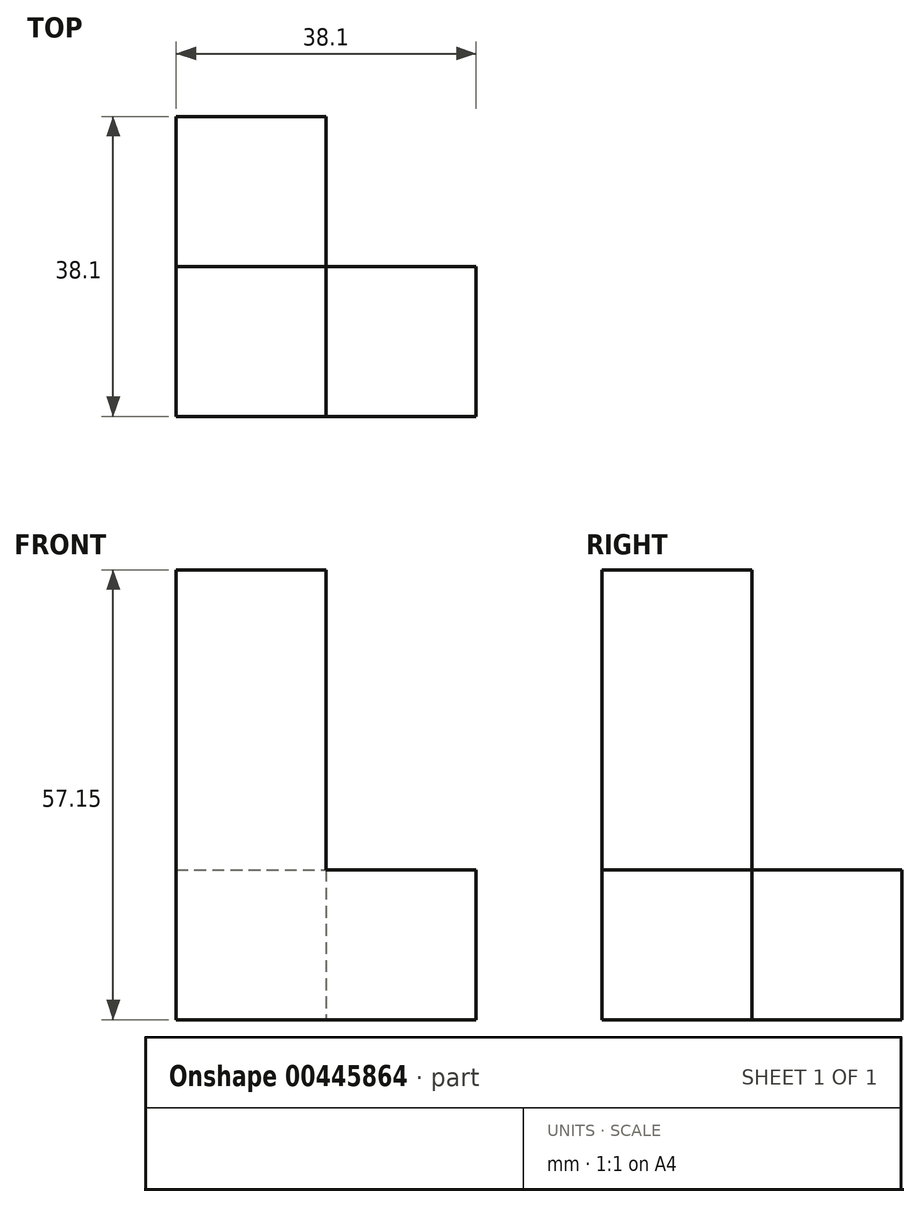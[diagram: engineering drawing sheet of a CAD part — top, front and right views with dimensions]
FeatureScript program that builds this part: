
annotation { "Feature Type Name" : "Feature", "Feature Type Description" : "" }
export const myFeature = defineFeature(function(context is Context, id is Id, definition is map)
    precondition{}
    {
        {
            var Q0;
            Q0=qCreatedBy(makeId("Top.planeOp"),FACE);
            var sketch = newSketch(context, id + "F0", { "sketchPlane" : qUnion([Q0])});
            skLineSegment(sketch, "E0.bottom", {"start": v(0, 0) * mm, "end": v(19.05, 0) * mm});
            skLineSegment(sketch, "E0.top", {"start": v(0, 19.05) * mm, "end": v(19.05, 19.05) * mm});
            skLineSegment(sketch, "E0.left", {"start": v(0, 0) * mm, "end": v(0, 19.05) * mm});
            skLineSegment(sketch, "E0.right", {"start": v(19.05, 0) * mm, "end": v(19.05, 19.05) * mm});
            skLineSegment(sketch, "E1.top", {"start": v(0, 38.1) * mm, "end": v(19.05, 38.1) * mm});
            skLineSegment(sketch, "E1.left", {"start": v(0, 19.05) * mm, "end": v(0, 38.1) * mm});
            skLineSegment(sketch, "E1.right", {"start": v(19.05, 19.05) * mm, "end": v(19.05, 38.1) * mm});
            skLineSegment(sketch, "E2.bottom", {"start": v(19.05, 0) * mm, "end": v(38.1, 0) * mm});
            skLineSegment(sketch, "E2.top", {"start": v(19.05, 19.05) * mm, "end": v(38.1, 19.05) * mm});
            skLineSegment(sketch, "E2.right", {"start": v(38.1, 0) * mm, "end": v(38.1, 19.05) * mm});
            skSolve(sketch);
        }
        {
            var Q0;
            Q0=makeQuery(id+"F0.imprint","IMPRINT",FACE,{"disambiguationData":[TD([[makeQuery(id+"F0.imprint","IMPRINT",EDGE,{"derivedFrom":sQuery(id+"F0.wireOp",EDGE,"E2.bottom")}),1.0]])]});
            var Q1;
            Q1=makeQuery(id+"F0.imprint","IMPRINT",FACE,{"disambiguationData":[TD([[makeQuery(id+"F0.imprint","IMPRINT",EDGE,{"derivedFrom":sQuery(id+"F0.wireOp",EDGE,"E0.bottom")}),1.0]])]});
            var Q2;
            Q2=makeQuery(id+"F0.imprint","IMPRINT",FACE,{"disambiguationData":[TD([[makeQuery(id+"F0.imprint","IMPRINT",EDGE,{"derivedFrom":sQuery(id+"F0.wireOp",EDGE,"E0.top")}),1.0]])]});
            extrude(context, id + "F1", {"entities" : qUnion([Q0, Q1, Q2]), "depth" : 19.05 * mm});
        }
        {
            var Q0;
            Q0=makeQuery(id+"F1.opExtrude","CAP_FACE",FACE,{"disambiguationData":[OSD([sQuery(id+"F0.wireOp",EDGE,"E0.bottom"),sQuery(id+"F0.wireOp",EDGE,"E0.left"),sQuery(id+"F0.wireOp",EDGE,"E1.top"),sQuery(id+"F0.wireOp",EDGE,"E1.left"),sQuery(id+"F0.wireOp",EDGE,"E1.right"),sQuery(id+"F0.wireOp",EDGE,"E2.bottom"),sQuery(id+"F0.wireOp",EDGE,"E2.top"),sQuery(id+"F0.wireOp",EDGE,"E2.right")])],"isStart":false});
            var sketch = newSketch(context, id + "F2", { "sketchPlane" : qUnion([Q0])});
            skLineSegment(sketch, "E3.bottom", {"start": v(0, 0) * mm, "end": v(19.05, 0) * mm});
            skLineSegment(sketch, "E3.top", {"start": v(0, 19.05) * mm, "end": v(19.05, 19.05) * mm});
            skLineSegment(sketch, "E3.left", {"start": v(0, 0) * mm, "end": v(0, 19.05) * mm});
            skLineSegment(sketch, "E3.right", {"start": v(19.05, 0) * mm, "end": v(19.05, 19.05) * mm});
            skSolve(sketch);
        }
        {
            var Q0;
            Q0=makeQuery(id+"F2.imprint","IMPRINT",FACE,{"disambiguationData":[TD([[makeQuery(id+"F2.imprint","IMPRINT",EDGE,{"derivedFrom":sQuery(id+"F2.wireOp",EDGE,"E3.bottom")}),1.0]])]});
            extrude(context, id + "F3", {"entities" : qUnion([Q0]), "operationType" : NewBodyOperationType.ADD, "depth" : 19.05 * mm * 2});
        }
    });
